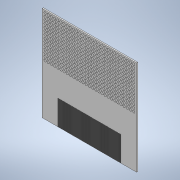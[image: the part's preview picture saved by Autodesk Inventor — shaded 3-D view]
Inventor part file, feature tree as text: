
AUTODESK INVENTOR PART (.ipt)
format: ipt  version: 2021 (Build 250183000, 183)  size: 941,568 bytes
history: native  units: in
note: dims shown in document units (in); Inventor stores cm internally (conversion verified against a paired STEP export)
features: extrude x3, sketch x3, pattern_linear x2, projected_geometry x2
ambient origin geometry x8: Origin, YZ Plane, XZ Plane, XY Plane, X Axis, Y Axis, Z Axis, Center Point
bodies: Solid1 (feature_tree)
feature tree (10):
  extrude  "Extrusion1"  Depth=2.9921in
  extrude  "Extrusion2"  Depth=0.0118in
  pattern_linear  "Rectangular Pattern1"  Count1=2  [1 undecoded]
  extrude  "Extrusion3"  Depth=0.0236in
  pattern_linear  "Rectangular Pattern2"  Count1=4  [1 undecoded]
  sketch  "Sketch1"  dims[d0=2.9921in d1=2.9921in]
  sketch  "Sketch2"  dims[d2=0.0394in d3=0.0in d4=0.0118in d5=0.7874in]
  projected_geometry  "Projected Loop1"
  sketch  "Sketch3"  dims[d6=0.0014in d7=0.0in d8=33.4646in d10=0.0236in d11=1.5748in d12=0.1969in d13=0.0787in d16=0.0014in d17=0.0in d18=0.0787in d19=11.4173in d21=0.1in d22=5.5118in d24=0.1in]
  projected_geometry  "Projected Loop2"
note: 2 required parameter values undecoded (feature->parameter linkage not recoverable at this tier; creation-order binding heuristic only, values carry confidence <= 0.55)
